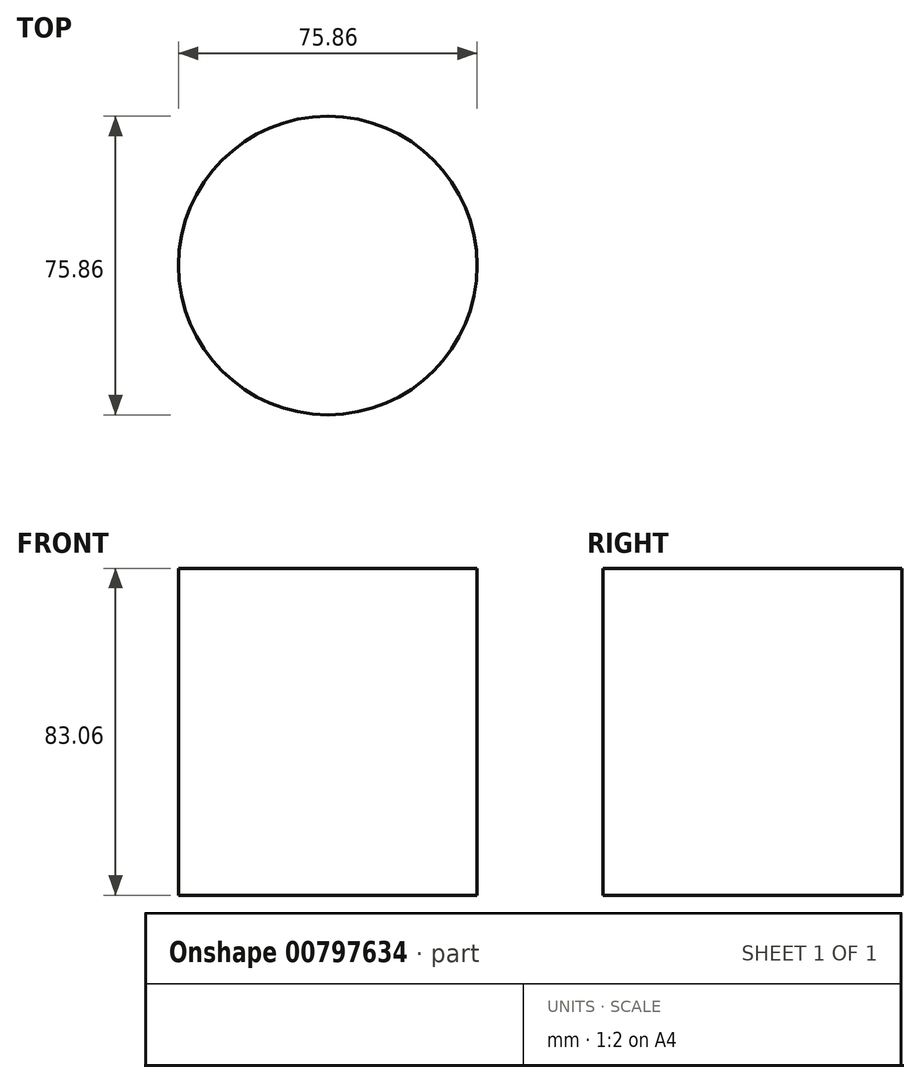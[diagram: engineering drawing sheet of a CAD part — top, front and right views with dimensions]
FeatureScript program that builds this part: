
annotation { "Feature Type Name" : "Feature", "Feature Type Description" : "" }
export const myFeature = defineFeature(function(context is Context, id is Id, definition is map)
    precondition{}
    {
        {
            var Q0;
            Q0=qCreatedBy(makeId("Top.planeOp"),FACE);
            var sketch = newSketch(context, id + "F0", { "sketchPlane" : qUnion([Q0])});
            skCircle(sketch, "E0", {"center": v(0, 0) * mm, "radius": 37.93 * mm});
            skSolve(sketch);
        }
        {
            var Q0;
            Q0 = qSketchRegion(id + "F0", true);
            extrude(context, id + "F1", {"entities" : qUnion([Q0]), "depth" : 83.06 * mm, "offsetDistance" : 25.4 * mm});
        }
    });
